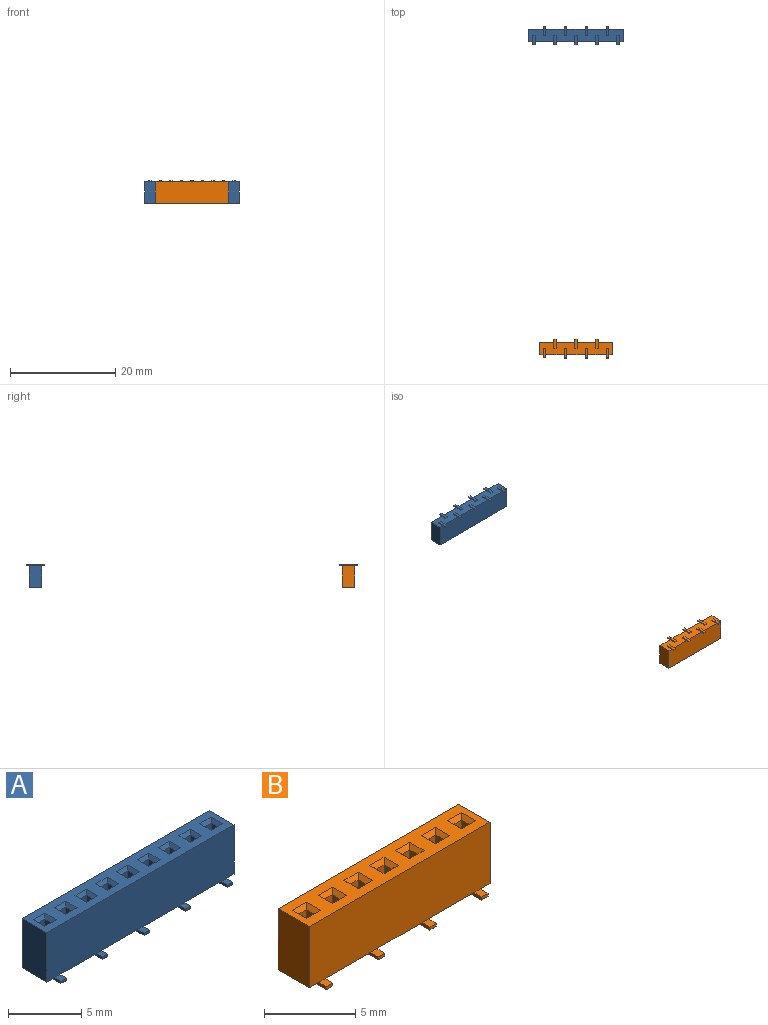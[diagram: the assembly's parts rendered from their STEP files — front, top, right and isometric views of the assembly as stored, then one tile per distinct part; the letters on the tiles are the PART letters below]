
ASSEMBLY  parts=2 mates=1
PART A: 141 faces, bbox 18x3.6x4.3 mm
  f0: plane 18x2.4mm, normal (0,0,-1), area 37.8mm2, adj f2,f3,f4,f5,f88,f90,f91,f93
  f1: plane 18x2.4mm, normal (0,0,1), area 32.3mm2, adj f2,f3,f4,f5,f51,f52,f53,f54
  f2: plane 18x4.1mm, normal (0,-1,0), area 73.8mm2, adj f0,f1,f3,f5,f87,f102,f108,f114
  f3: plane 4.1x2.4mm, normal (-1,0,0), area 9.8mm2, adj f0,f1,f2,f4
  f4: plane 18x4.1mm, normal (0,1,0), area 73.8mm2, adj f0,f1,f3,f5,f96,f126,f132,f138
  f5: plane 4.1x2.4mm, normal (1,0,0), area 9.8mm2, adj f0,f1,f2,f4
  f6: plane 3.25x0.6mm, normal (1,0,0), area 2mm2, adj f7,f9,f10,f80
  f7: plane 3.25x0.6mm, normal (0,1,0), area 1.9mm2, adj f6,f8,f9,f82
  f8: plane 3.25x0.6mm, normal (-1,0,0), area 2mm2, adj f7,f9,f10,f81
  f9: plane 0.6x0.6mm, normal (0,0,1), area 0.4mm2, adj f6,f7,f8,f10
  f10: plane 3.25x0.6mm, normal (0,-1,0), area 1.9mm2, adj f6,f8,f9,f79
  f11: plane 3.25x0.6mm, normal (1,0,0), area 2mm2, adj f12,f14,f15,f56
  f12: plane 3.25x0.6mm, normal (0,1,0), area 1.9mm2, adj f11,f13,f14,f58
  f13: plane 3.25x0.6mm, normal (-1,0,0), area 2mm2, adj f12,f14,f15,f57
  f14: plane 0.6x0.6mm, normal (0,0,1), area 0.4mm2, adj f11,f12,f13,f15
  f15: plane 3.25x0.6mm, normal (0,-1,0), area 1.9mm2, adj f11,f13,f14,f55
  f16: plane 3.25x0.6mm, normal (1,0,0), area 2mm2, adj f17,f19,f20,f52
  f17: plane 3.25x0.6mm, normal (0,1,0), area 1.9mm2, adj f16,f18,f19,f54
  f18: plane 3.25x0.6mm, normal (-1,0,0), area 2mm2, adj f17,f19,f20,f53
  f19: plane 0.6x0.6mm, normal (0,0,1), area 0.4mm2, adj f16,f17,f18,f20
  f20: plane 3.25x0.6mm, normal (0,-1,0), area 1.9mm2, adj f16,f18,f19,f51
  f21: plane 3.25x0.6mm, normal (1,0,0), area 2mm2, adj f22,f24,f25,f76
  f22: plane 3.25x0.6mm, normal (0,1,0), area 1.9mm2, adj f21,f23,f24,f78
  f23: plane 3.25x0.6mm, normal (-1,0,0), area 2mm2, adj f22,f24,f25,f77
  f24: plane 0.6x0.6mm, normal (0,0,1), area 0.4mm2, adj f21,f22,f23,f25
  f25: plane 3.25x0.6mm, normal (0,-1,0), area 1.9mm2, adj f21,f23,f24,f75
  f26: plane 3.25x0.6mm, normal (1,0,0), area 2mm2, adj f27,f29,f30,f72
  f27: plane 3.25x0.6mm, normal (0,1,0), area 1.9mm2, adj f26,f28,f29,f74
  f28: plane 3.25x0.6mm, normal (-1,0,0), area 2mm2, adj f27,f29,f30,f73
  f29: plane 0.6x0.6mm, normal (0,0,1), area 0.4mm2, adj f26,f27,f28,f30
  f30: plane 3.25x0.6mm, normal (0,-1,0), area 1.9mm2, adj f26,f28,f29,f71
  f31: plane 3.25x0.6mm, normal (1,0,0), area 2mm2, adj f32,f34,f35,f64
  f32: plane 3.25x0.6mm, normal (0,1,0), area 1.9mm2, adj f31,f33,f34,f66
  f33: plane 3.25x0.6mm, normal (-1,0,0), area 2mm2, adj f32,f34,f35,f65
  f34: plane 0.6x0.6mm, normal (0,0,1), area 0.4mm2, adj f31,f32,f33,f35
  f35: plane 3.25x0.6mm, normal (0,-1,0), area 1.9mm2, adj f31,f33,f34,f63
  f36: plane 3.25x0.6mm, normal (1,0,0), area 2mm2, adj f37,f39,f40,f60
  f37: plane 3.25x0.6mm, normal (0,1,0), area 1.9mm2, adj f36,f38,f39,f62
  f38: plane 3.25x0.6mm, normal (-1,0,0), area 2mm2, adj f37,f39,f40,f61
  f39: plane 0.6x0.6mm, normal (0,0,1), area 0.4mm2, adj f36,f37,f38,f40
  f40: plane 3.25x0.6mm, normal (0,-1,0), area 1.9mm2, adj f36,f38,f39,f59
  f41: plane 3.25x0.6mm, normal (1,0,0), area 2mm2, adj f42,f44,f45,f68
  f42: plane 3.25x0.6mm, normal (0,1,0), area 1.9mm2, adj f41,f43,f44,f70
  f43: plane 3.25x0.6mm, normal (-1,0,0), area 2mm2, adj f42,f44,f45,f69
  f44: plane 0.6x0.6mm, normal (0,0,1), area 0.4mm2, adj f41,f42,f43,f45
  f45: plane 3.25x0.6mm, normal (0,-1,0), area 1.9mm2, adj f41,f43,f44,f67
  f46: plane 3.25x0.6mm, normal (1,0,0), area 2mm2, adj f47,f49,f50,f84
  f47: plane 3.25x0.6mm, normal (0,1,0), area 1.9mm2, adj f46,f48,f49,f86
  f48: plane 3.25x0.6mm, normal (-1,0,0), area 2mm2, adj f47,f49,f50,f85
  f49: plane 0.6x0.6mm, normal (0,0,1), area 0.4mm2, adj f46,f47,f48,f50
  f50: plane 3.25x0.6mm, normal (0,-1,0), area 1.9mm2, adj f46,f48,f49,f83
  f51: plane 1.1x0.25mm, normal (0,-0.71,0.71), area 0.3mm2, adj f1,f20,f52,f53
  f52: plane 1.1x0.25mm, normal (0.71,0,0.71), area 0.3mm2, adj f1,f16,f51,f54
  f53: plane 1.1x0.25mm, normal (-0.71,0,0.71), area 0.3mm2, adj f1,f18,f51,f54
  f54: plane 1.1x0.25mm, normal (0,0.71,0.71), area 0.3mm2, adj f1,f17,f52,f53
  f55: plane 1.1x0.25mm, normal (0,-0.71,0.71), area 0.3mm2, adj f1,f15,f56,f57
  f56: plane 1.1x0.25mm, normal (0.71,0,0.71), area 0.3mm2, adj f1,f11,f55,f58
  f57: plane 1.1x0.25mm, normal (-0.71,0,0.71), area 0.3mm2, adj f1,f13,f55,f58
  f58: plane 1.1x0.25mm, normal (0,0.71,0.71), area 0.3mm2, adj f1,f12,f56,f57
  f59: plane 1.1x0.25mm, normal (0,-0.71,0.71), area 0.3mm2, adj f1,f40,f60,f61
  f60: plane 1.1x0.25mm, normal (0.71,0,0.71), area 0.3mm2, adj f1,f36,f59,f62
  f61: plane 1.1x0.25mm, normal (-0.71,0,0.71), area 0.3mm2, adj f1,f38,f59,f62
  f62: plane 1.1x0.25mm, normal (0,0.71,0.71), area 0.3mm2, adj f1,f37,f60,f61
  f63: plane 1.1x0.25mm, normal (0,-0.71,0.71), area 0.3mm2, adj f1,f35,f64,f65
  f64: plane 1.1x0.25mm, normal (0.71,0,0.71), area 0.3mm2, adj f1,f31,f63,f66
  f65: plane 1.1x0.25mm, normal (-0.71,0,0.71), area 0.3mm2, adj f1,f33,f63,f66
  f66: plane 1.1x0.25mm, normal (0,0.71,0.71), area 0.3mm2, adj f1,f32,f64,f65
  f67: plane 1.1x0.25mm, normal (0,-0.71,0.71), area 0.3mm2, adj f1,f45,f68,f69
  f68: plane 1.1x0.25mm, normal (0.71,0,0.71), area 0.3mm2, adj f1,f41,f67,f70
  f69: plane 1.1x0.25mm, normal (-0.71,0,0.71), area 0.3mm2, adj f1,f43,f67,f70
  f70: plane 1.1x0.25mm, normal (0,0.71,0.71), area 0.3mm2, adj f1,f42,f68,f69
  f71: plane 1.1x0.25mm, normal (0,-0.71,0.71), area 0.3mm2, adj f1,f30,f72,f73
  f72: plane 1.1x0.25mm, normal (0.71,0,0.71), area 0.3mm2, adj f1,f26,f71,f74
  f73: plane 1.1x0.25mm, normal (-0.71,0,0.71), area 0.3mm2, adj f1,f28,f71,f74
  f74: plane 1.1x0.25mm, normal (0,0.71,0.71), area 0.3mm2, adj f1,f27,f72,f73
  f75: plane 1.1x0.25mm, normal (0,-0.71,0.71), area 0.3mm2, adj f1,f25,f76,f77
  f76: plane 1.1x0.25mm, normal (0.71,0,0.71), area 0.3mm2, adj f1,f21,f75,f78
  f77: plane 1.1x0.25mm, normal (-0.71,0,0.71), area 0.3mm2, adj f1,f23,f75,f78
  f78: plane 1.1x0.25mm, normal (0,0.71,0.71), area 0.3mm2, adj f1,f22,f76,f77
  f79: plane 1.1x0.25mm, normal (0,-0.71,0.71), area 0.3mm2, adj f1,f10,f80,f81
  f80: plane 1.1x0.25mm, normal (0.71,0,0.71), area 0.3mm2, adj f1,f6,f79,f82
  f81: plane 1.1x0.25mm, normal (-0.71,0,0.71), area 0.3mm2, adj f1,f8,f79,f82
  f82: plane 1.1x0.25mm, normal (0,0.71,0.71), area 0.3mm2, adj f1,f7,f80,f81
  f83: plane 1.1x0.25mm, normal (0,-0.71,0.71), area 0.3mm2, adj f1,f50,f84,f85
  f84: plane 1.1x0.25mm, normal (0.71,0,0.71), area 0.3mm2, adj f1,f46,f83,f86
  f85: plane 1.1x0.25mm, normal (-0.71,0,0.71), area 0.3mm2, adj f1,f48,f83,f86
  f86: plane 1.1x0.25mm, normal (0,0.71,0.71), area 0.3mm2, adj f1,f47,f84,f85
  f87: plane 0.6x0.5mm, normal (0,0,1), area 0.3mm2, adj f2,f88,f89,f90
  f88: plane 1.8x0.2mm, normal (-1,0,0), area 0.4mm2, adj f0,f87,f89,f91,f92
  f89: plane 0.5x0.2mm, normal (0,-1,0), area 0.1mm2, adj f87,f88,f90,f92
  f90: plane 1.8x0.2mm, normal (1,0,0), area 0.4mm2, adj f0,f87,f89,f91,f92
  f91: plane 0.5x0.2mm, normal (0,1,0), area 0.1mm2, adj f0,f88,f90,f92
  f92: plane 1.8x0.5mm, normal (0,0,-1), area 0.9mm2, adj f88,f89,f90,f91
  f93: plane 1.8x0.2mm, normal (-1,0,0), area 0.4mm2, adj f0,f94,f96,f97,f98
  f94: plane 0.5x0.2mm, normal (0,-1,0), area 0.1mm2, adj f0,f93,f95,f98
  f95: plane 1.8x0.2mm, normal (1,0,0), area 0.4mm2, adj f0,f94,f96,f97,f98
  f96: plane 0.6x0.5mm, normal (0,0,1), area 0.3mm2, adj f4,f93,f95,f97
  f97: plane 0.5x0.2mm, normal (0,1,0), area 0.1mm2, adj f93,f95,f96,f98
  f98: plane 1.8x0.5mm, normal (0,0,-1), area 0.9mm2, adj f93,f94,f95,f97
  f99: plane 1.8x0.2mm, normal (-1,0,0), area 0.4mm2, adj f0,f100,f102,f103,f104
  f100: plane 0.5x0.2mm, normal (0,-1,0), area 0.1mm2, adj f99,f101,f102,f104
  f101: plane 1.8x0.2mm, normal (1,0,0), area 0.4mm2, adj f0,f100,f102,f103,f104
  f102: plane 0.6x0.5mm, normal (0,0,1), area 0.3mm2, adj f2,f99,f100,f101
  f103: plane 0.5x0.2mm, normal (0,1,0), area 0.1mm2, adj f0,f99,f101,f104
  f104: plane 1.8x0.5mm, normal (0,0,-1), area 0.9mm2, adj f99,f100,f101,f103
  f105: plane 1.8x0.2mm, normal (-1,0,0), area 0.4mm2, adj f0,f106,f108,f109,f110
  f106: plane 0.5x0.2mm, normal (0,-1,0), area 0.1mm2, adj f105,f107,f108,f110
  f107: plane 1.8x0.2mm, normal (1,0,0), area 0.4mm2, adj f0,f106,f108,f109,f110
  f108: plane 0.6x0.5mm, normal (0,0,1), area 0.3mm2, adj f2,f105,f106,f107
  f109: plane 0.5x0.2mm, normal (0,1,0), area 0.1mm2, adj f0,f105,f107,f110
  f110: plane 1.8x0.5mm, normal (0,0,-1), area 0.9mm2, adj f105,f106,f107,f109
  f111: plane 1.8x0.2mm, normal (-1,0,0), area 0.4mm2, adj f0,f112,f114,f115,f116
  f112: plane 0.5x0.2mm, normal (0,-1,0), area 0.1mm2, adj f111,f113,f114,f116
  f113: plane 1.8x0.2mm, normal (1,0,0), area 0.4mm2, adj f0,f112,f114,f115,f116
  f114: plane 0.6x0.5mm, normal (0,0,1), area 0.3mm2, adj f2,f111,f112,f113
  f115: plane 0.5x0.2mm, normal (0,1,0), area 0.1mm2, adj f0,f111,f113,f116
  f116: plane 1.8x0.5mm, normal (0,0,-1), area 0.9mm2, adj f111,f112,f113,f115
  f117: plane 1.8x0.2mm, normal (-1,0,0), area 0.4mm2, adj f0,f118,f120,f121,f122
  f118: plane 0.5x0.2mm, normal (0,-1,0), area 0.1mm2, adj f117,f119,f120,f122
  f119: plane 1.8x0.2mm, normal (1,0,0), area 0.4mm2, adj f0,f118,f120,f121,f122
  f120: plane 0.6x0.5mm, normal (0,0,1), area 0.3mm2, adj f2,f117,f118,f119
  f121: plane 0.5x0.2mm, normal (0,1,0), area 0.1mm2, adj f0,f117,f119,f122
  f122: plane 1.8x0.5mm, normal (0,0,-1), area 0.9mm2, adj f117,f118,f119,f121
  f123: plane 1.8x0.2mm, normal (-1,0,0), area 0.4mm2, adj f0,f124,f126,f127,f128
  f124: plane 0.5x0.2mm, normal (0,-1,0), area 0.1mm2, adj f0,f123,f125,f128
  f125: plane 1.8x0.2mm, normal (1,0,0), area 0.4mm2, adj f0,f124,f126,f127,f128
  f126: plane 0.6x0.5mm, normal (0,0,1), area 0.3mm2, adj f4,f123,f125,f127
  f127: plane 0.5x0.2mm, normal (0,1,0), area 0.1mm2, adj f123,f125,f126,f128
  f128: plane 1.8x0.5mm, normal (0,0,-1), area 0.9mm2, adj f123,f124,f125,f127
  f129: plane 1.8x0.2mm, normal (-1,0,0), area 0.4mm2, adj f0,f130,f132,f133,f134
  f130: plane 0.5x0.2mm, normal (0,-1,0), area 0.1mm2, adj f0,f129,f131,f134
  f131: plane 1.8x0.2mm, normal (1,0,0), area 0.4mm2, adj f0,f130,f132,f133,f134
  f132: plane 0.6x0.5mm, normal (0,0,1), area 0.3mm2, adj f4,f129,f131,f133
  f133: plane 0.5x0.2mm, normal (0,1,0), area 0.1mm2, adj f129,f131,f132,f134
  f134: plane 1.8x0.5mm, normal (0,0,-1), area 0.9mm2, adj f129,f130,f131,f133
  f135: plane 1.8x0.2mm, normal (-1,0,0), area 0.4mm2, adj f0,f136,f138,f139,f140
  f136: plane 0.5x0.2mm, normal (0,-1,0), area 0.1mm2, adj f0,f135,f137,f140
  f137: plane 1.8x0.2mm, normal (1,0,0), area 0.4mm2, adj f0,f136,f138,f139,f140
  f138: plane 0.6x0.5mm, normal (0,0,1), area 0.3mm2, adj f4,f135,f137,f139
  f139: plane 0.5x0.2mm, normal (0,1,0), area 0.1mm2, adj f135,f137,f138,f140
  f140: plane 1.8x0.5mm, normal (0,0,-1), area 0.9mm2, adj f135,f136,f137,f139
PART B: 111 faces, bbox 14x3.6x4.3 mm
  f0: plane 14x2.4mm, normal (0,0,-1), area 29.4mm2, adj f2,f3,f4,f5,f70,f72,f73,f75
  f1: plane 14x2.4mm, normal (0,0,1), area 25.1mm2, adj f2,f3,f4,f5,f41,f42,f43,f44
  f2: plane 14x4.1mm, normal (0,-1,0), area 57.4mm2, adj f0,f1,f3,f5,f69,f84,f90,f96
  f3: plane 4.1x2.4mm, normal (-1,0,0), area 9.8mm2, adj f0,f1,f2,f4
  f4: plane 14x4.1mm, normal (0,1,0), area 57.4mm2, adj f0,f1,f3,f5,f78,f102,f108
  f5: plane 4.1x2.4mm, normal (1,0,0), area 9.8mm2, adj f0,f1,f2,f4
  f6: plane 3.25x0.6mm, normal (1,0,0), area 2mm2, adj f7,f9,f10,f42
  f7: plane 3.25x0.6mm, normal (0,1,0), area 1.9mm2, adj f6,f8,f9,f44
  f8: plane 3.25x0.6mm, normal (-1,0,0), area 2mm2, adj f7,f9,f10,f43
  f9: plane 0.6x0.6mm, normal (0,0,1), area 0.4mm2, adj f6,f7,f8,f10
  f10: plane 3.25x0.6mm, normal (0,-1,0), area 1.9mm2, adj f6,f8,f9,f41
  f11: plane 3.25x0.6mm, normal (1,0,0), area 2mm2, adj f12,f14,f15,f62
  f12: plane 3.25x0.6mm, normal (0,1,0), area 1.9mm2, adj f11,f13,f14,f64
  f13: plane 3.25x0.6mm, normal (-1,0,0), area 2mm2, adj f12,f14,f15,f63
  f14: plane 0.6x0.6mm, normal (0,0,1), area 0.4mm2, adj f11,f12,f13,f15
  f15: plane 3.25x0.6mm, normal (0,-1,0), area 1.9mm2, adj f11,f13,f14,f61
  f16: plane 3.25x0.6mm, normal (1,0,0), area 2mm2, adj f17,f19,f20,f66
  f17: plane 3.25x0.6mm, normal (0,1,0), area 1.9mm2, adj f16,f18,f19,f68
  f18: plane 3.25x0.6mm, normal (-1,0,0), area 2mm2, adj f17,f19,f20,f67
  f19: plane 0.6x0.6mm, normal (0,0,1), area 0.4mm2, adj f16,f17,f18,f20
  f20: plane 3.25x0.6mm, normal (0,-1,0), area 1.9mm2, adj f16,f18,f19,f65
  f21: plane 3.25x0.6mm, normal (1,0,0), area 2mm2, adj f22,f24,f25,f46
  f22: plane 3.25x0.6mm, normal (0,1,0), area 1.9mm2, adj f21,f23,f24,f48
  f23: plane 3.25x0.6mm, normal (-1,0,0), area 2mm2, adj f22,f24,f25,f47
  f24: plane 0.6x0.6mm, normal (0,0,1), area 0.4mm2, adj f21,f22,f23,f25
  f25: plane 3.25x0.6mm, normal (0,-1,0), area 1.9mm2, adj f21,f23,f24,f45
  f26: plane 3.25x0.6mm, normal (1,0,0), area 2mm2, adj f27,f29,f30,f50
  f27: plane 3.25x0.6mm, normal (0,1,0), area 1.9mm2, adj f26,f28,f29,f52
  f28: plane 3.25x0.6mm, normal (-1,0,0), area 2mm2, adj f27,f29,f30,f51
  f29: plane 0.6x0.6mm, normal (0,0,1), area 0.4mm2, adj f26,f27,f28,f30
  f30: plane 3.25x0.6mm, normal (0,-1,0), area 1.9mm2, adj f26,f28,f29,f49
  f31: plane 3.25x0.6mm, normal (1,0,0), area 2mm2, adj f32,f34,f35,f58
  f32: plane 3.25x0.6mm, normal (0,1,0), area 1.9mm2, adj f31,f33,f34,f60
  f33: plane 3.25x0.6mm, normal (-1,0,0), area 2mm2, adj f32,f34,f35,f59
  f34: plane 0.6x0.6mm, normal (0,0,1), area 0.4mm2, adj f31,f32,f33,f35
  f35: plane 3.25x0.6mm, normal (0,-1,0), area 1.9mm2, adj f31,f33,f34,f57
  f36: plane 3.25x0.6mm, normal (1,0,0), area 2mm2, adj f37,f39,f40,f54
  f37: plane 3.25x0.6mm, normal (0,1,0), area 1.9mm2, adj f36,f38,f39,f56
  f38: plane 3.25x0.6mm, normal (-1,0,0), area 2mm2, adj f37,f39,f40,f55
  f39: plane 0.6x0.6mm, normal (0,0,1), area 0.4mm2, adj f36,f37,f38,f40
  f40: plane 3.25x0.6mm, normal (0,-1,0), area 1.9mm2, adj f36,f38,f39,f53
  f41: plane 1.1x0.25mm, normal (0,-0.71,0.71), area 0.3mm2, adj f1,f10,f42,f43
  f42: plane 1.1x0.25mm, normal (0.71,0,0.71), area 0.3mm2, adj f1,f6,f41,f44
  f43: plane 1.1x0.25mm, normal (-0.71,0,0.71), area 0.3mm2, adj f1,f8,f41,f44
  f44: plane 1.1x0.25mm, normal (0,0.71,0.71), area 0.3mm2, adj f1,f7,f42,f43
  f45: plane 1.1x0.25mm, normal (0,-0.71,0.71), area 0.3mm2, adj f1,f25,f46,f47
  f46: plane 1.1x0.25mm, normal (0.71,0,0.71), area 0.3mm2, adj f1,f21,f45,f48
  f47: plane 1.1x0.25mm, normal (-0.71,0,0.71), area 0.3mm2, adj f1,f23,f45,f48
  f48: plane 1.1x0.25mm, normal (0,0.71,0.71), area 0.3mm2, adj f1,f22,f46,f47
  f49: plane 1.1x0.25mm, normal (0,-0.71,0.71), area 0.3mm2, adj f1,f30,f50,f51
  f50: plane 1.1x0.25mm, normal (0.71,0,0.71), area 0.3mm2, adj f1,f26,f49,f52
  f51: plane 1.1x0.25mm, normal (-0.71,0,0.71), area 0.3mm2, adj f1,f28,f49,f52
  f52: plane 1.1x0.25mm, normal (0,0.71,0.71), area 0.3mm2, adj f1,f27,f50,f51
  f53: plane 1.1x0.25mm, normal (0,-0.71,0.71), area 0.3mm2, adj f1,f40,f54,f55
  f54: plane 1.1x0.25mm, normal (0.71,0,0.71), area 0.3mm2, adj f1,f36,f53,f56
  f55: plane 1.1x0.25mm, normal (-0.71,0,0.71), area 0.3mm2, adj f1,f38,f53,f56
  f56: plane 1.1x0.25mm, normal (0,0.71,0.71), area 0.3mm2, adj f1,f37,f54,f55
  f57: plane 1.1x0.25mm, normal (0,-0.71,0.71), area 0.3mm2, adj f1,f35,f58,f59
  f58: plane 1.1x0.25mm, normal (0.71,0,0.71), area 0.3mm2, adj f1,f31,f57,f60
  f59: plane 1.1x0.25mm, normal (-0.71,0,0.71), area 0.3mm2, adj f1,f33,f57,f60
  f60: plane 1.1x0.25mm, normal (0,0.71,0.71), area 0.3mm2, adj f1,f32,f58,f59
  f61: plane 1.1x0.25mm, normal (0,-0.71,0.71), area 0.3mm2, adj f1,f15,f62,f63
  f62: plane 1.1x0.25mm, normal (0.71,0,0.71), area 0.3mm2, adj f1,f11,f61,f64
  f63: plane 1.1x0.25mm, normal (-0.71,0,0.71), area 0.3mm2, adj f1,f13,f61,f64
  f64: plane 1.1x0.25mm, normal (0,0.71,0.71), area 0.3mm2, adj f1,f12,f62,f63
  f65: plane 1.1x0.25mm, normal (0,-0.71,0.71), area 0.3mm2, adj f1,f20,f66,f67
  f66: plane 1.1x0.25mm, normal (0.71,0,0.71), area 0.3mm2, adj f1,f16,f65,f68
  f67: plane 1.1x0.25mm, normal (-0.71,0,0.71), area 0.3mm2, adj f1,f18,f65,f68
  f68: plane 1.1x0.25mm, normal (0,0.71,0.71), area 0.3mm2, adj f1,f17,f66,f67
  f69: plane 0.6x0.5mm, normal (0,0,1), area 0.3mm2, adj f2,f70,f71,f72
  f70: plane 1.8x0.2mm, normal (-1,0,0), area 0.4mm2, adj f0,f69,f71,f73,f74
  f71: plane 0.5x0.2mm, normal (0,-1,0), area 0.1mm2, adj f69,f70,f72,f74
  f72: plane 1.8x0.2mm, normal (1,0,0), area 0.4mm2, adj f0,f69,f71,f73,f74
  f73: plane 0.5x0.2mm, normal (0,1,0), area 0.1mm2, adj f0,f70,f72,f74
  f74: plane 1.8x0.5mm, normal (0,0,-1), area 0.9mm2, adj f70,f71,f72,f73
  f75: plane 1.8x0.2mm, normal (-1,0,0), area 0.4mm2, adj f0,f76,f78,f79,f80
  f76: plane 0.5x0.2mm, normal (0,-1,0), area 0.1mm2, adj f0,f75,f77,f80
  f77: plane 1.8x0.2mm, normal (1,0,0), area 0.4mm2, adj f0,f76,f78,f79,f80
  f78: plane 0.6x0.5mm, normal (0,0,1), area 0.3mm2, adj f4,f75,f77,f79
  f79: plane 0.5x0.2mm, normal (0,1,0), area 0.1mm2, adj f75,f77,f78,f80
  f80: plane 1.8x0.5mm, normal (0,0,-1), area 0.9mm2, adj f75,f76,f77,f79
  f81: plane 1.8x0.2mm, normal (-1,0,0), area 0.4mm2, adj f0,f82,f84,f85,f86
  f82: plane 0.5x0.2mm, normal (0,-1,0), area 0.1mm2, adj f81,f83,f84,f86
  f83: plane 1.8x0.2mm, normal (1,0,0), area 0.4mm2, adj f0,f82,f84,f85,f86
  f84: plane 0.6x0.5mm, normal (0,0,1), area 0.3mm2, adj f2,f81,f82,f83
  f85: plane 0.5x0.2mm, normal (0,1,0), area 0.1mm2, adj f0,f81,f83,f86
  f86: plane 1.8x0.5mm, normal (0,0,-1), area 0.9mm2, adj f81,f82,f83,f85
  f87: plane 1.8x0.2mm, normal (-1,0,0), area 0.4mm2, adj f0,f88,f90,f91,f92
  f88: plane 0.5x0.2mm, normal (0,-1,0), area 0.1mm2, adj f87,f89,f90,f92
  f89: plane 1.8x0.2mm, normal (1,0,0), area 0.4mm2, adj f0,f88,f90,f91,f92
  f90: plane 0.6x0.5mm, normal (0,0,1), area 0.3mm2, adj f2,f87,f88,f89
  f91: plane 0.5x0.2mm, normal (0,1,0), area 0.1mm2, adj f0,f87,f89,f92
  f92: plane 1.8x0.5mm, normal (0,0,-1), area 0.9mm2, adj f87,f88,f89,f91
  f93: plane 1.8x0.2mm, normal (-1,0,0), area 0.4mm2, adj f0,f94,f96,f97,f98
  f94: plane 0.5x0.2mm, normal (0,-1,0), area 0.1mm2, adj f93,f95,f96,f98
  f95: plane 1.8x0.2mm, normal (1,0,0), area 0.4mm2, adj f0,f94,f96,f97,f98
  f96: plane 0.6x0.5mm, normal (0,0,1), area 0.3mm2, adj f2,f93,f94,f95
  f97: plane 0.5x0.2mm, normal (0,1,0), area 0.1mm2, adj f0,f93,f95,f98
  f98: plane 1.8x0.5mm, normal (0,0,-1), area 0.9mm2, adj f93,f94,f95,f97
  f99: plane 1.8x0.2mm, normal (-1,0,0), area 0.4mm2, adj f0,f100,f102,f103,f104
  f100: plane 0.5x0.2mm, normal (0,-1,0), area 0.1mm2, adj f0,f99,f101,f104
  f101: plane 1.8x0.2mm, normal (1,0,0), area 0.4mm2, adj f0,f100,f102,f103,f104
  f102: plane 0.6x0.5mm, normal (0,0,1), area 0.3mm2, adj f4,f99,f101,f103
  f103: plane 0.5x0.2mm, normal (0,1,0), area 0.1mm2, adj f99,f101,f102,f104
  f104: plane 1.8x0.5mm, normal (0,0,-1), area 0.9mm2, adj f99,f100,f101,f103
  f105: plane 1.8x0.2mm, normal (-1,0,0), area 0.4mm2, adj f0,f106,f108,f109,f110
  f106: plane 0.5x0.2mm, normal (0,-1,0), area 0.1mm2, adj f0,f105,f107,f110
  f107: plane 1.8x0.2mm, normal (1,0,0), area 0.4mm2, adj f0,f106,f108,f109,f110
  f108: plane 0.6x0.5mm, normal (0,0,1), area 0.3mm2, adj f4,f105,f107,f109
  f109: plane 0.5x0.2mm, normal (0,1,0), area 0.1mm2, adj f105,f107,f108,f110
  f110: plane 1.8x0.5mm, normal (0,0,-1), area 0.9mm2, adj f105,f106,f107,f109
PLACE A rot(axis=(0,-1,0),180deg) t=(9,-1.2,4.1)mm
PLACE B rot(axis=(0,-1,0),180deg) t=(7,-60.7,4.1)mm
MATE planar A.f1 <-> B.f1  axis (0,0,-1) through (0,0,0)mm
